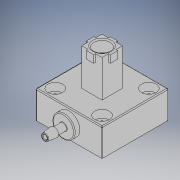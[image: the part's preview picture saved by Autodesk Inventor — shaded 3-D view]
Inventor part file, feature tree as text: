
AUTODESK INVENTOR PART (.ipt)
format: ipt  version: 2019 (Build 230136000, 136)  size: 310,784 bytes
history: native  units: mm
features: sketch x9, extrude x4, plane x3, revolve x2, fillet x2, projected_geometry x2, sweep x1, hole x1, pattern_circular x1
ambient origin geometry x8: Origin, YZ Plane, XZ Plane, XY Plane, X Axis, Y Axis, Z Axis, Center Point
bodies: Solid1 (feature_tree)
feature tree (25):
  revolve  "Revolution1"  [1 undecoded]
  plane  "Work Plane1"
  extrude  "Extrusion1"  Depth=0.75mm
  plane  "Work Plane7"
  extrude  "Extrusion6"  Depth=0.75mm
  extrude  "Extrusion7"  TaperAngle=0.0deg  [1 undecoded]
  sketch  "Sketch17"  dims[d14=2.0mm d15=0.0mm d45=0.0mm d47=15.0mm d48=0.0mm]
  plane  "Work Plane8"
  sweep  "Sweep3"
  fillet  "Fillet1"  Radius=15.0mm
  hole  "Hole3"  [1 undecoded]
  revolve  "Revolution2"  [1 undecoded]
  fillet  "Fillet2"  [1 undecoded]
  extrude  "Extrusion13"  Depth=3.0mm
  pattern_circular  "Circular Pattern1"  [2 undecoded]
  sketch  "Sketch1"  dims[d1=20.0mm d5=9.0mm]
  sketch  "Sketch2"  dims[d6=0.35mm d7=0.75mm]
  sketch  "Sketch11"  dims[d8=0.75mm d9=0.75mm]
  sketch  "Sketch16"  dims[d10=90.0deg d11=0.0mm]
  projected_geometry  "Projected Loop9"
  sketch  "Sketch18"  dims[d60=36.0mm d61=36.0mm]
  sketch  "Sketch19"  dims[d64=8.45mm d65=32.7mm d66=0.0mm d67=0.0mm d68=0.0mm]
  sketch  "Sketch21"  dims[d69=3.0mm d70=25.4mm]
  sketch  "Sketch28"  dims[d71=25.4mm d72=4.496mm d73=6.0mm d74=7.938mm d75=4.166mm d76=90.0deg d77=19.05mm d78=20.594885mm d79=3.0mm d80=6.0mm d81=5.0mm d82=1.8796mm d83=0.25mm d84=2.413mm d85=5.08mm d86=1.15mm d87=0.25mm d88=0.25mm d89=90.0deg d90=0.5mm d124=0.0mm d125=0.0mm d126=4.0mm d127=1.0mm d128=0.0mm d129=40.0mm d130=360.0deg d133=5.5mm d134=1.013632mm]
  projected_geometry  "Projected Loop13"
note: 7 required parameter values undecoded (feature->parameter linkage not recoverable at this tier; creation-order binding heuristic only, values carry confidence <= 0.55)